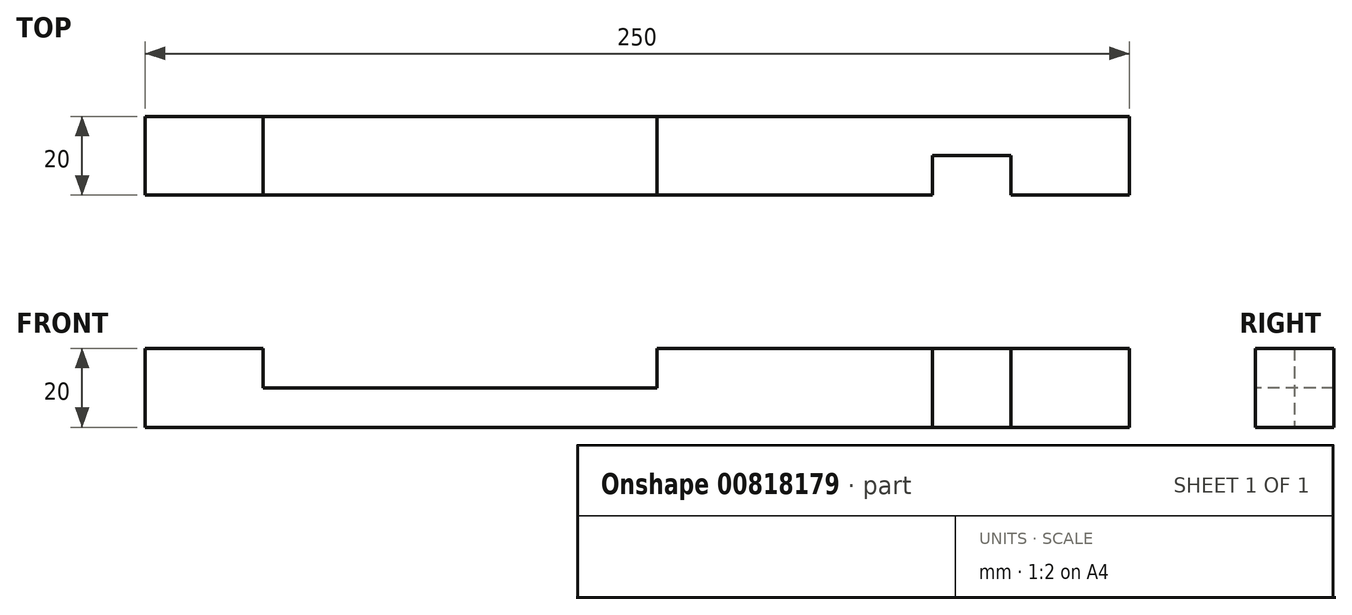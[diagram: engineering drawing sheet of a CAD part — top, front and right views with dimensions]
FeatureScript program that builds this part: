
annotation { "Feature Type Name" : "Feature", "Feature Type Description" : "" }
export const myFeature = defineFeature(function(context is Context, id is Id, definition is map)
    precondition{}
    {
        {
            var Q0;
            Q0=qCreatedBy(makeId("Top.planeOp"),FACE);
            var sketch = newSketch(context, id + "F0", { "sketchPlane" : qUnion([Q0])});
            skLineSegment(sketch, "E0.bottom", {"start": v(125, -10) * mm, "end": v(-125, -10) * mm});
            skLineSegment(sketch, "E0.top", {"start": v(125, 10) * mm, "end": v(-125, 10) * mm});
            skLineSegment(sketch, "E0.left", {"start": v(125, -10) * mm, "end": v(125, 10) * mm});
            skLineSegment(sketch, "E0.right", {"start": v(-125, -10) * mm, "end": v(-125, 10) * mm});
            skPoint(sketch, "E0.middle", {"position": v(0, 0) * mm});
            skSolve(sketch);
        }
        {
            var Q0;
            Q0=makeQuery(id+"F0.imprint","IMPRINT",FACE,{"disambiguationData":[TD([[makeQuery(id+"F0.imprint","IMPRINT",EDGE,{"derivedFrom":sQuery(id+"F0.wireOp",EDGE,"E0.bottom")}),-1.0]])]});
            extrude(context, id + "F1", {"entities" : qUnion([Q0]), "depth" : 20 * mm, "offsetDistance" : 25 * mm});
        }
        {
            var Q0;
            Q0=makeQuery(id+"F1.opExtrude","SWEPT_FACE",FACE,{"disambiguationData":[OSD([sQuery(id+"F0.wireOp",EDGE,"E0.bottom")])]});
            var sketch = newSketch(context, id + "F2", { "sketchPlane" : qUnion([Q0])});
            skLineSegment(sketch, "E1", {"start": v(95, 20) * mm, "end": v(95, 0) * mm});
            skLineSegment(sketch, "E2", {"start": v(95, 0) * mm, "end": v(75, 0) * mm});
            skLineSegment(sketch, "E3", {"start": v(75, 0) * mm, "end": v(75, 20) * mm});
            skLineSegment(sketch, "E4", {"start": v(75, 20) * mm, "end": v(95, 20) * mm});
            skSolve(sketch);
        }
        {
            var Q0;
            Q0=makeQuery(id+"F2.imprint","IMPRINT",FACE,{"disambiguationData":[TD([[makeQuery(id+"F2.imprint","IMPRINT",EDGE,{"derivedFrom":sQuery(id+"F2.wireOp",EDGE,"E1")}),-1.0]])]});
            extrude(context, id + "F3", {"entities" : qUnion([Q0]), "operationType" : NewBodyOperationType.REMOVE, "oppositeDirection" : true, "depth" : 10 * mm, "offsetDistance" : 25 * mm});
        }
        {
            var Q0;
            Q0=makeQuery(id+"F1.opExtrude","CAP_FACE",FACE,{"disambiguationData":[OSD([sQuery(id+"F0.wireOp",EDGE,"E0.bottom"),sQuery(id+"F0.wireOp",EDGE,"E0.top"),sQuery(id+"F0.wireOp",EDGE,"E0.left"),sQuery(id+"F0.wireOp",EDGE,"E0.right")])],"isStart":false});
            var sketch = newSketch(context, id + "F4", { "sketchPlane" : qUnion([Q0])});
            skLineSegment(sketch, "E5", {"start": v(-95, 10) * mm, "end": v(-95, -10) * mm});
            skLineSegment(sketch, "E6", {"start": v(-95, -10) * mm, "end": v(5, -10) * mm});
            skLineSegment(sketch, "E7", {"start": v(5, 10) * mm, "end": v(-95, 10) * mm});
            skLineSegment(sketch, "E8", {"start": v(5, -10) * mm, "end": v(5, 10) * mm});
            skSolve(sketch);
        }
        {
            var Q0;
            Q0=makeQuery(id+"F4.imprint","IMPRINT",FACE,{"disambiguationData":[TD([[makeQuery(id+"F4.imprint","IMPRINT",EDGE,{"derivedFrom":sQuery(id+"F4.wireOp",EDGE,"E5")}),1.0]])]});
            extrude(context, id + "F5", {"entities" : qUnion([Q0]), "operationType" : NewBodyOperationType.REMOVE, "oppositeDirection" : true, "depth" : 10 * mm, "offsetDistance" : 25 * mm});
        }
    });
